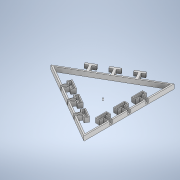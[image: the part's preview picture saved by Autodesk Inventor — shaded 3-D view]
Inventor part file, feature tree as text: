
AUTODESK INVENTOR PART (.ipt)
format: ipt  version: 2022.3 (Build 263350000, 350)  size: 541,696 bytes
history: native  units: mm
features: extrude x7, thicken_offset x6, sketch x5, hole x1, projected_geometry x1
ambient origin geometry x8: Origin, YZ Plane, XZ Plane, XY Plane, X Axis, Y Axis, Z Axis, Center Point
bodies: Solid1 (feature_tree)
feature tree (20):
  sketch  "Sketch1"  dims[d1=200.0mm d2=35.0mm]
  extrude  "Extrusion1"  Depth=35.0mm
  extrude  "Extrusion2"  Depth=5.0mm
  extrude  "Extrusion3"  Depth=40.0mm
  extrude  "Extrusion4"  Depth=10.0mm TaperAngle=0.0deg
  sketch  "Sketch3"  dims[d5=20.0mm d6=30.0mm d8=40.0mm d9=30.0mm d11=40.0mm]
  extrude  "Extrusion6"  Depth=22.0mm
  extrude  "Extrusion7"  Depth=3.0mm
  hole  "Hole1"  [1 undecoded]
  thicken_offset  "Thicken1"
  thicken_offset  "Thicken2"
  thicken_offset  "Thicken3"
  thicken_offset  "Thicken4"
  thicken_offset  "Thicken5"
  thicken_offset  "Thicken6"
  extrude  "Extrusion8"  Depth=15.0mm
  sketch  "Sketch2"  dims[d3=5.0mm d4=5.0mm]
  projected_geometry  "Projected Loop1"
  sketch  "Sketch4"  dims[d14=10.0mm d15=0.0mm d16=10.0mm d17=0.0mm]
  sketch  "Sketch5"  dims[d18=2.2mm d19=0.0mm d20=22.0mm d21=3.0mm d22=1.5mm d23=0.0mm d24=15.0mm d25=120.0deg d26=10.0mm d27=5.0mm d28=20.0mm d29=90.0deg d30=5.0mm d31=2.5mm d32=5.0mm d33=20.0mm d35=120.0deg d37=30.0mm d39=40.0mm d40=30.0mm d42=40.0mm d45=30.0mm d47=40.0mm d48=30.0mm d50=40.0mm d55=7.8mm d56=0.0mm d57=10.0mm d58=0.0mm d59=40.0mm d60=2.2mm d61=6.0mm d62=3.1mm d63=4.1mm d64=90.0deg d65=2.2mm d66=0.0mm d67=0.1mm d68=0.05mm d69=0.1mm d70=0.05mm d71=0.1mm d72=0.05mm d73=0.1mm d74=0.05mm d75=0.1mm d76=0.05mm d77=0.1mm d78=0.05mm d79=3.0mm d80=38.2mm d81=24.2mm d82=20.0mm d84=40.0mm d85=20.0mm d87=40.0mm d90=20.0mm d92=240.0deg d94=0.0mm d95=0.0mm d96=9.9mm d97=7.5mm d98=9.9mm d99=7.5mm d100=20.0mm d102=40.0mm d103=20.0mm d105=40.0mm d108=20.0mm d110=240.0deg]
note: 1 required parameter value undecoded (feature->parameter linkage not recoverable at this tier; creation-order binding heuristic only, values carry confidence <= 0.55)
